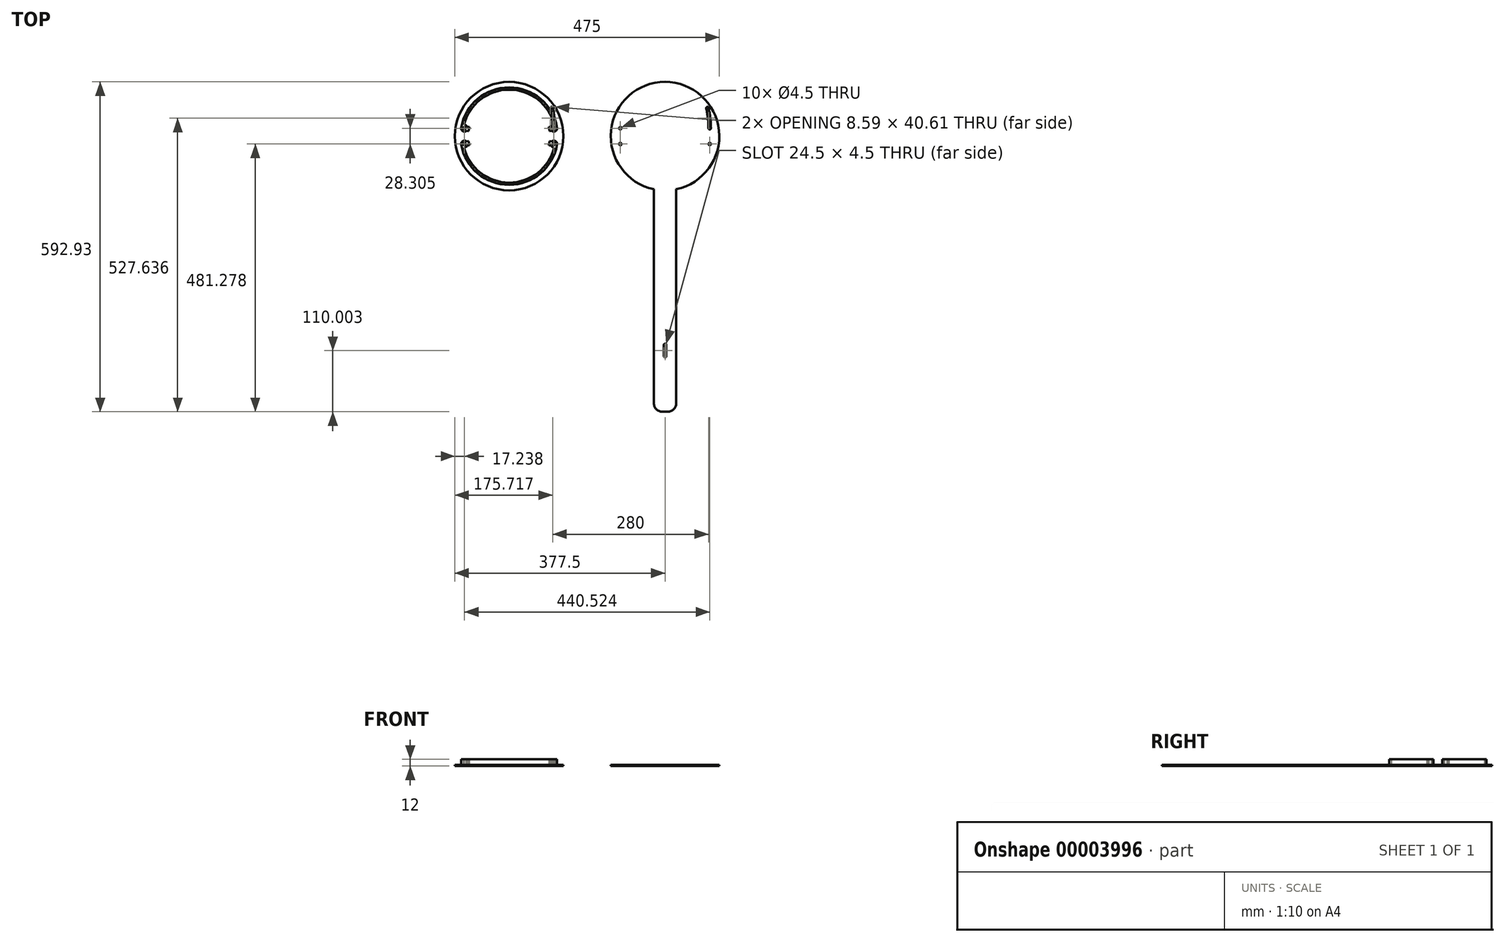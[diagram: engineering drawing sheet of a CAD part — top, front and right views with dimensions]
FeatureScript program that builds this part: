
annotation { "Feature Type Name" : "Feature", "Feature Type Description" : "" }
export const myFeature = defineFeature(function(context is Context, id is Id, definition is map)
    precondition{}
    {
        {
            var Q0;
            Q0=qCreatedBy(makeId("Top.planeOp"),FACE);
            var sketch = newSketch(context, id + "F0", { "sketchPlane" : qUnion([Q0])});
            skCircle(sketch, "E0", {"center": v(0, 0) * mm, "radius": 95.5 * mm});
            skCircle(sketch, "E1", {"center": v(0, 0) * mm, "radius": 83.5 * mm});
            skCircle(sketch, "E2", {"center": v(0, 0) * mm, "radius": 87.5 * mm});
            skLineSegment(sketch, "E3", {"start": v(-95.5, 0) * mm, "end": v(95.5, 0) * mm});
            skLineSegment(sketch, "E4", {"start": v(0, 0) * mm, "end": v(-94.05, 16.58) * mm});
            skCircle(sketch, "E5", {"center": v(-80.26, 14.15) * mm, "radius": 2.25 * mm});
            skCircle(sketch, "E6", {"center": v(-80.26, 14.15) * mm, "radius": 6 * mm});
            skLineSegment(sketch, "E7", {"start": v(0, 0) * mm, "end": v(0, 95.5) * mm});
            skLineSegment(sketch, "E8", {"start": v(-71.92, 12.68) * mm, "end": v(-71.22, 16.62) * mm});
            skLineSegment(sketch, "E9", {"start": v(-71.22, 16.62) * mm, "end": v(-75.16, 17.31) * mm});
            skLineSegment(sketch, "E10.MirrorCS", {"start": v(-71.92, 12.68) * mm, "end": v(-72.61, 8.74) * mm});
            skLineSegment(sketch, "E11.MirrorCS", {"start": v(-72.61, 8.74) * mm, "end": v(-76.55, 9.44) * mm});
            skSolve(sketch);
        }
        {
            var Q0;
            {var subQ0=sQuery(id+"F0.wireOp",EDGE,"E7");var subQ3=sQuery(id+"F0.wireOp",EDGE,"E1");var subQ4=makeQuery(id+"F0.imprint","INTERSECT",VERTEX,{"derivedFrom":[subQ3,subQ0]});Q0=makeQuery(id+"F0.imprint","IMPRINT",FACE,{"disambiguationData":[TD([[makeQuery(id+"F0.imprint","IMPRINT",EDGE,{"disambiguationData":[TD([[subQ4,-1.0]])],"derivedFrom":subQ3}),-1.0]])]});}
            var Q1;
            {var subQ0=sQuery(id+"F0.wireOp",EDGE,"E6");var subQ3=sQuery(id+"F0.wireOp",EDGE,"E1");var subQ4=makeQuery(id+"F0.imprint","INTERSECT",VERTEX,{"disambiguationData":[OD(0.0)],"derivedFrom":[subQ3,subQ0]});Q1=makeQuery(id+"F0.imprint","IMPRINT",FACE,{"disambiguationData":[TD([[makeQuery(id+"F0.imprint","IMPRINT",EDGE,{"disambiguationData":[TD([[subQ4,-1.0]])],"derivedFrom":subQ3}),-1.0]])]});}
            var Q2;
            {var subQ0=sQuery(id+"F0.wireOp",EDGE,"E6");var subQ3=sQuery(id+"F0.wireOp",EDGE,"E1");var subQ4=makeQuery(id+"F0.imprint","INTERSECT",VERTEX,{"disambiguationData":[OD(0.0)],"derivedFrom":[subQ3,subQ0]});Q2=makeQuery(id+"F0.imprint","IMPRINT",FACE,{"disambiguationData":[TD([[makeQuery(id+"F0.imprint","IMPRINT",EDGE,{"disambiguationData":[TD([[subQ4,-1.0]])],"derivedFrom":subQ3}),1.0]])]});}
            var Q3;
            {var subQ3=sQuery(id+"F0.wireOp",EDGE,"E1");var subQ5=sQuery(id+"F0.wireOp",EDGE,"E5");var subQ7=makeQuery(id+"F0.imprint","INTERSECT",VERTEX,{"disambiguationData":[OD(1.0)],"derivedFrom":[subQ3,subQ5]});Q3=makeQuery(id+"F0.imprint","IMPRINT",FACE,{"disambiguationData":[TD([[makeQuery(id+"F0.imprint","IMPRINT",EDGE,{"disambiguationData":[TD([[subQ7,-1.0]])],"derivedFrom":subQ3}),1.0]])]});}
            var Q4;
            {var subQ0=sQuery(id+"F0.wireOp",EDGE,"E5");var subQ3=sQuery(id+"F0.wireOp",EDGE,"E1");var subQ4=makeQuery(id+"F0.imprint","INTERSECT",VERTEX,{"disambiguationData":[OD(1.0)],"derivedFrom":[subQ3,subQ0]});Q4=makeQuery(id+"F0.imprint","IMPRINT",FACE,{"disambiguationData":[TD([[makeQuery(id+"F0.imprint","IMPRINT",EDGE,{"disambiguationData":[TD([[subQ4,-1.0]])],"derivedFrom":subQ3}),-1.0]])]});}
            var Q5;
            {var subQ1=sQuery(id+"F0.wireOp",EDGE,"E10.MirrorCS");Q5=makeQuery(id+"F0.imprint","IMPRINT",FACE,{"disambiguationData":[TD([[makeQuery(id+"F0.imprint","IMPRINT",EDGE,{"derivedFrom":subQ1}),-1.0]])]});}
            var Q6;
            {var subQ1=sQuery(id+"F0.wireOp",EDGE,"E8");Q6=makeQuery(id+"F0.imprint","IMPRINT",FACE,{"disambiguationData":[TD([[makeQuery(id+"F0.imprint","IMPRINT",EDGE,{"derivedFrom":subQ1}),1.0]])]});}
            extrude(context, id + "F1", {"entities" : qUnion([Q0, Q1, Q2, Q3, Q4, Q5, Q6]), "depth" : 10 * mm});
        }
        {
            var Q0;
            Q0=makeQuery(id+"F1.opExtrude","SWEPT_BODY",BODY,{"disambiguationData":[OSD([sQuery(id+"F0.wireOp",EDGE,"E1"),sQuery(id+"F0.wireOp",EDGE,"E2"),sQuery(id+"F0.wireOp",EDGE,"E5"),sQuery(id+"F0.wireOp",EDGE,"E6"),sQuery(id+"F0.wireOp",EDGE,"E7")])]});
            var Q1;
            Q1=makeQuery(id+"F1.opExtrude","SWEPT_FACE",FACE,{"disambiguationData":[OSD([sQuery(id+"F0.wireOp",EDGE,"E7")])]});
            mirror(context, id + "F2", {"operationType" : NewBodyOperationType.ADD, "entities" : qUnion([Q0]), "mirrorPlane" : qUnion([Q1])});
        }
        {
            var Q0;
            Q0=makeQuery(id+"F1.opExtrude","SWEPT_BODY",BODY,{"disambiguationData":[OSD([sQuery(id+"F0.wireOp",EDGE,"E1"),sQuery(id+"F0.wireOp",EDGE,"E2"),sQuery(id+"F0.wireOp",EDGE,"E5"),sQuery(id+"F0.wireOp",EDGE,"E6"),sQuery(id+"F0.wireOp",EDGE,"E7"),sQuery(id+"F0.wireOp",EDGE,"E8"),sQuery(id+"F0.wireOp",EDGE,"E9"),sQuery(id+"F0.wireOp",EDGE,"E10.MirrorCS"),sQuery(id+"F0.wireOp",EDGE,"E11.MirrorCS")])]});
            var Q1;
            Q1=qCreatedBy(makeId("Front.planeOp"),FACE);
            mirror(context, id + "F3", {"entities" : qUnion([Q0]), "mirrorPlane" : qUnion([Q1])});
        }
        {
            var Q0;
            Q0=qCreatedBy(makeId("Top.planeOp"),FACE);
            var sketch = newSketch(context, id + "F4", { "sketchPlane" : qUnion([Q0])});
            skCircle(sketch, "E12", {"center": v(0, 0) * mm, "radius": 97.5 * mm});
            skCircle(sketch, "E13.0", {"center": v(-80.26, -14.15) * mm, "radius": 2.25 * mm});
            skCircle(sketch, "E14.0", {"center": v(-80.26, 14.15) * mm, "radius": 2.25 * mm});
            skCircle(sketch, "E15.0", {"center": v(80.26, -14.15) * mm, "radius": 2.25 * mm});
            skCircle(sketch, "E16.0", {"center": v(80.26, 14.15) * mm, "radius": 2.25 * mm});
            skCircle(sketch, "E17", {"center": v(-80.26, 14.15) * mm, "radius": 160.52 * mm, "construction": true});
            skCircle(sketch, "E18", {"center": v(76.14, 50.29) * mm, "radius": 2.25 * mm});
            skArc(sketch, "E19", {"start": v(82.51, 14.15) * mm, "mid": v(81.46, 32.6) * mm, "end": v(78.33, 50.8) * mm});
            skArc(sketch, "E20", {"start": v(78.01, 14.15) * mm, "mid": v(77, 32.08) * mm, "end": v(73.95, 49.78) * mm});
            skSolve(sketch);
        }
        {
            var Q0;
            Q0=makeQuery(id+"F4.imprint","IMPRINT",FACE,{"disambiguationData":[TD([[makeQuery(id+"F4.imprint","IMPRINT",EDGE,{"derivedFrom":sQuery(id+"F4.wireOp",EDGE,"E12")}),1.0]])]});
            var Q1;
            {var subQ1=sQuery(id+"F4.wireOp",EDGE,"e646a2dc-60d2-475b-8d70-19e72077c876");Q1=makeQuery(id+"F4.imprint","IMPRINT",FACE,{"disambiguationData":[TD([[makeQuery(id+"F4.imprint","IMPRINT",EDGE,{"derivedFrom":subQ1}),-1.0]])]});}
            extrude(context, id + "F5", {"entities" : qUnion([Q0, Q1]), "oppositeDirection" : true, "depth" : 2 * mm});
        }
        {
            var Q0;
            Q0=makeQuery(id+"F5.opExtrude","SWEPT_BODY",BODY,{"disambiguationData":[OSD([sQuery(id+"F4.wireOp",EDGE,"E12"),sQuery(id+"F4.wireOp",EDGE,"E13.0"),sQuery(id+"F4.wireOp",EDGE,"E14.0"),sQuery(id+"F4.wireOp",EDGE,"E15.0"),sQuery(id+"F4.wireOp",EDGE,"E16.0"),sQuery(id+"F4.wireOp",EDGE,"E18"),sQuery(id+"F4.wireOp",EDGE,"E19"),sQuery(id+"F4.wireOp",EDGE,"E20"),sQuery(id+"F4.wireOp",EDGE,"e646a2dc-60d2-475b-8d70-19e72077c876"),sQuery(id+"F4.wireOp",EDGE,"21cee253-5297-4bd4-a44f-7b46ea9f8b61"),sQuery(id+"F4.wireOp",EDGE,"46b259f5-49ee-4d25-82ff-222f7e6a29720.MirrorCS"),sQuery(id+"F4.wireOp",EDGE,"9ae59bea-2eeb-403d-8ac5-4b24ffd4b14f0.MirrorCS")])]});
            transform(context, id + "F6", {"entities" : qUnion([Q0]), "transformType" : TransformType.TRANSLATION_3D, "dx" : 280 * mm, "dy" : 0 * mm, "dz" : 0 * mm, "makeCopy" : true});
        }
        {
            var Q0;
            Q0=makeQuery(id+"F6.opPattern","COPY",FACE,{"derivedFrom":makeQuery(id+"F5.opExtrude","CAP_FACE",FACE,{"disambiguationData":[OSD([sQuery(id+"F4.wireOp",EDGE,"E12"),sQuery(id+"F4.wireOp",EDGE,"E13.0"),sQuery(id+"F4.wireOp",EDGE,"E14.0"),sQuery(id+"F4.wireOp",EDGE,"E15.0"),sQuery(id+"F4.wireOp",EDGE,"E16.0"),sQuery(id+"F4.wireOp",EDGE,"E18"),sQuery(id+"F4.wireOp",EDGE,"E19"),sQuery(id+"F4.wireOp",EDGE,"E20")])],"isStart":true}),"instanceName":"1"});
            var sketch = newSketch(context, id + "F7", { "sketchPlane" : qUnion([Q0])});
            skLineSegment(sketch, "E21", {"start": v(280, 0) * mm, "end": v(280, -495.43) * mm, "construction": true});
            skLineSegment(sketch, "E22", {"start": v(280, -495.43) * mm, "end": v(260, -495.43) * mm});
            skLineSegment(sketch, "E23", {"start": v(260, -495.43) * mm, "end": v(260, -95.43) * mm});
            skLineSegment(sketch, "E24.MirrorCS", {"start": v(300, -495.43) * mm, "end": v(300, -95.43) * mm});
            skLineSegment(sketch, "E25.MirrorCS", {"start": v(280, -495.43) * mm, "end": v(300, -495.43) * mm});
            skCircle(sketch, "E26", {"center": v(280, -375.43) * mm, "radius": 2.25 * mm});
            skCircle(sketch, "E27", {"center": v(280, -395.43) * mm, "radius": 2.25 * mm});
            skLineSegment(sketch, "E28", {"start": v(277.75, -395.43) * mm, "end": v(277.75, -375.43) * mm});
            skLineSegment(sketch, "E29", {"start": v(282.25, -395.43) * mm, "end": v(282.25, -375.43) * mm});
            skSolve(sketch);
        }
        {
            var Q0;
            Q0=makeQuery(id+"F7.imprint","IMPRINT",FACE,{"disambiguationData":[TD([[makeQuery(id+"F7.imprint","IMPRINT",EDGE,{"derivedFrom":sQuery(id+"F7.wireOp",EDGE,"E22")}),-1.0]])]});
            var Q1;
            Q1=makeQuery(id+"F6.opPattern","COPY",FACE,{"derivedFrom":makeQuery(id+"F5.opExtrude","CAP_FACE",FACE,{"disambiguationData":[OSD([sQuery(id+"F4.wireOp",EDGE,"E12"),sQuery(id+"F4.wireOp",EDGE,"E13.0"),sQuery(id+"F4.wireOp",EDGE,"E14.0"),sQuery(id+"F4.wireOp",EDGE,"E15.0"),sQuery(id+"F4.wireOp",EDGE,"E16.0"),sQuery(id+"F4.wireOp",EDGE,"E18"),sQuery(id+"F4.wireOp",EDGE,"E19"),sQuery(id+"F4.wireOp",EDGE,"E20")])],"isStart":false}),"instanceName":"1"});
            extrude(context, id + "F8", {"entities" : qUnion([Q0]), "operationType" : NewBodyOperationType.ADD, "endBound" : BoundingType.UP_TO_SURFACE, "oppositeDirection" : true, "endBoundEntityFace" : qUnion([Q1]), "depth" : 25 * mm});
        }
        {
            var Q0;
            Q0=makeQuery(id+"F8.opExtrude","SWEPT_EDGE",EDGE,{"disambiguationData":[OSD([sQuery(id+"F7.wireOp",EDGE,"E24.MirrorCS"),sQuery(id+"F7.wireOp",EDGE,"E25.MirrorCS")])]});
            var Q1;
            Q1=makeQuery(id+"F8.opExtrude","SWEPT_EDGE",EDGE,{"disambiguationData":[OSD([sQuery(id+"F7.wireOp",EDGE,"E22"),sQuery(id+"F7.wireOp",EDGE,"E23")])]});
            var Q2;
            Q2=makeQuery(id+"F8.opExtrude","SWEPT_EDGE",EDGE,{"disambiguationData":[OSD([sQuery(id+"F4.wireOp",EDGE,"E12"),sQuery(id+"F7.wireOp",EDGE,"E24.MirrorCS")])]});
            var Q3;
            Q3=makeQuery(id+"F8.opExtrude","SWEPT_EDGE",EDGE,{"disambiguationData":[OSD([sQuery(id+"F4.wireOp",EDGE,"E12"),sQuery(id+"F7.wireOp",EDGE,"E23")])]});
            fillet(context, id + "F9", {"entities" : qUnion([Q0, Q1, Q2, Q3]), "radius" : 15 * mm, "tangentPropagation" : true, "allowEdgeOverflow" : false});
        }
    });
